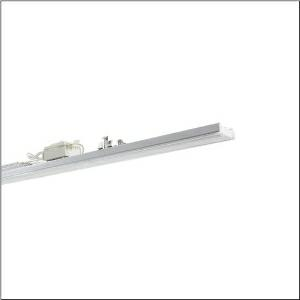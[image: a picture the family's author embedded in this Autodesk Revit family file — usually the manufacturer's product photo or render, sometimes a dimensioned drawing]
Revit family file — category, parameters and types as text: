
# Revit family: licross_11_recessed_mo_51te12mn4axg
name_source: partatom
category: Lighting Fixtures
units: mm (PartAtom-declared; Revit-internal decimal feet)

## family parameters
Cut with Voids When Loaded = No
Host = Face
Light Source = No
Part Type = Normal
Room Calculation Point = No
Round Connector Dimension = Use Diameter
Shared = No

## types (1)
- --- (1 x LED, 10290 lm, 55.2 W, 4000K)
    Apparent Load = 55 VA
    CIE Flux Codes = 67 92 99 100 100
    Color Rendering = 80
    Color Temperature = 4000K
    Default Elevation = 1800 mm
    Description = Licross 11 Recessed MO, luminaire insert, of sheet steel, galvanised, coil coated, white, length: 1.500mm, width: 66mm, height: 67mm, LED rated luminous flux: 10.290lm, light colour: 840, SDCM (Standard Deviation of Colour Matching)MacAdam ≤ 2 SDCM (initial), control gear: ON/OFF Multilumen, with plug, 3-pole, with phase selection, mains connection: 220..240V, AC, 50/60Hz, rated input power: 55W, internal wiring halogen-free, primary optical cover: cover, of PMMA, light emission: direct distribution, primary light characteristic: symmetric, protection rating (complete): IP54, insulation class (complete): insulation class I (protective earthing), certification: CE, ENEC, VDE, UKCA, protection symbol: D if used in an environment with non-conductive dust loads with corresponding accessories, impact resistance: IK06, permissible ambient temperature for indoor applications: -35..+40°C, corresponds to IFS (International Featured Standards) requirements for safety and quality in the food industry, reducing of maximum allowable ambient temperature of 5°C with ceiling mounting, The light source and the operating device comply with the requirements of the Ecodesign Regulation (EU) 2019/2020 and are replaceable in accordance with this regulation, packaging unit: 1 piece
    Height = 58 mm
    Lamp = 1 x LED
    Lamp Light Flux = 10290 lm
    Lamp Power = 55.2 W
    Lamp count = 1
    Length = 1500 mm
    Luminous efficacy = 186 lm/W
    Manufacturer = Siteco
    ModVariant = No
    Model = 51TE12MN4AXG
    Mounting Place = Ceiling
    Mounting Type = Pendant
    Number of Poles = 1
    OnlyDefault = Yes
    Power Factor = 1
    Product Name = Licross 11 Recessed MO
    Product group = luminaire insert | ceiling pendant
    ProductGroupID = 901
    Protection Class = Protection class I
    Protection Degree = IP 54
    RLX_Detail_Level = 1
    RLX_Emergency_Light_Flux = 0 lm
    RLX_Emergency_Type = 0
    RLX_Emergency_Type_DB = No
    RlxData = <blob elided: 22385 chars, md5=5af69d3d>
    Socket = socket
    Standby Power = 0 W
    System Light Flux = 10290 lm
    System Power = 55 W
    Type Comments = factory setting: luminous flux: 100 % | (A | C | E) | 126 mA
    Type Image = l_1296930.jpg
    URL = http://relux.com
    VarID = @adj_090281
    Voltage = 0 V
    Weight = 0.00 kg
    Width = 66 mm

## geometry (parser evidence)
native form markers: Blend x4, Sweep x12
no freeform markers — native parametric forms only
